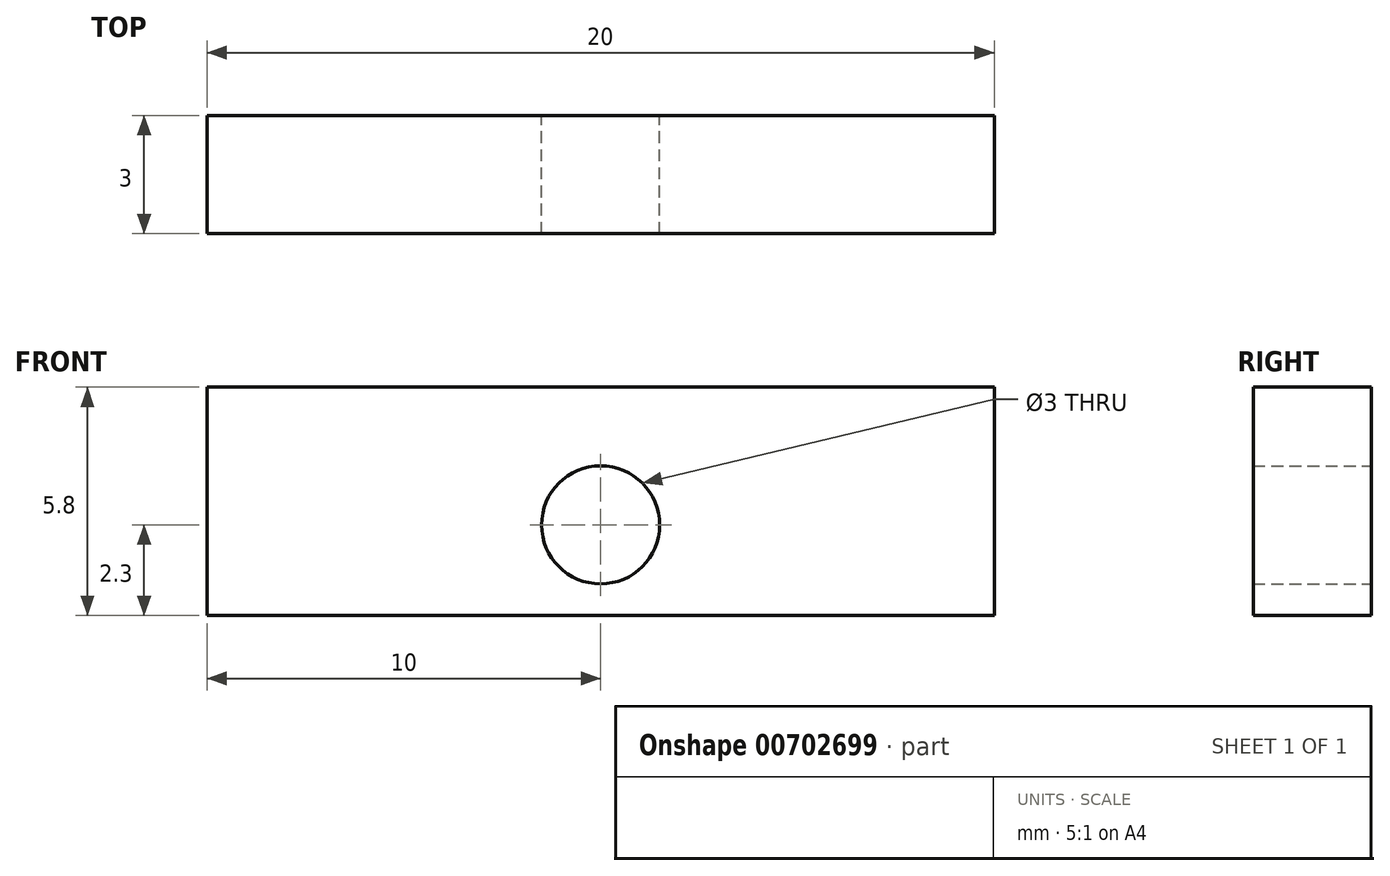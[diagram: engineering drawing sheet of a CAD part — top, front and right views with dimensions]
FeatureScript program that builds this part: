
annotation { "Feature Type Name" : "Feature", "Feature Type Description" : "" }
export const myFeature = defineFeature(function(context is Context, id is Id, definition is map)
    precondition{}
    {
        {
            var Q0;
            Q0=qCreatedBy(makeId("Front.planeOp"),FACE);
            var sketch = newSketch(context, id + "F0", { "sketchPlane" : qUnion([Q0])});
            skCircle(sketch, "E0", {"center": v(0, 0) * mm, "radius": 1.5 * mm});
            skLineSegment(sketch, "E1.bottom", {"start": v(-10, 3.5) * mm, "end": v(10, 3.5) * mm});
            skLineSegment(sketch, "E1.top", {"start": v(-10, -2.3) * mm, "end": v(10, -2.3) * mm});
            skLineSegment(sketch, "E1.left", {"start": v(-10, 3.5) * mm, "end": v(-10, -2.3) * mm});
            skLineSegment(sketch, "E1.right", {"start": v(10, 3.5) * mm, "end": v(10, -2.3) * mm});
            skPoint(sketch, "E2", {"position": v(0, 3.5) * mm});
            skSolve(sketch);
        }
        {
            var Q0;
            Q0=makeQuery(id+"F0.imprint","IMPRINT",FACE,{"disambiguationData":[TD([[makeQuery(id+"F0.imprint","IMPRINT",EDGE,{"derivedFrom":sQuery(id+"F0.wireOp",EDGE,"E0")}),-1.0]])]});
            extrude(context, id + "F1", {"entities" : qUnion([Q0]), "depth" : 3 * mm, "offsetDistance" : 25.4 * mm});
        }
    });
